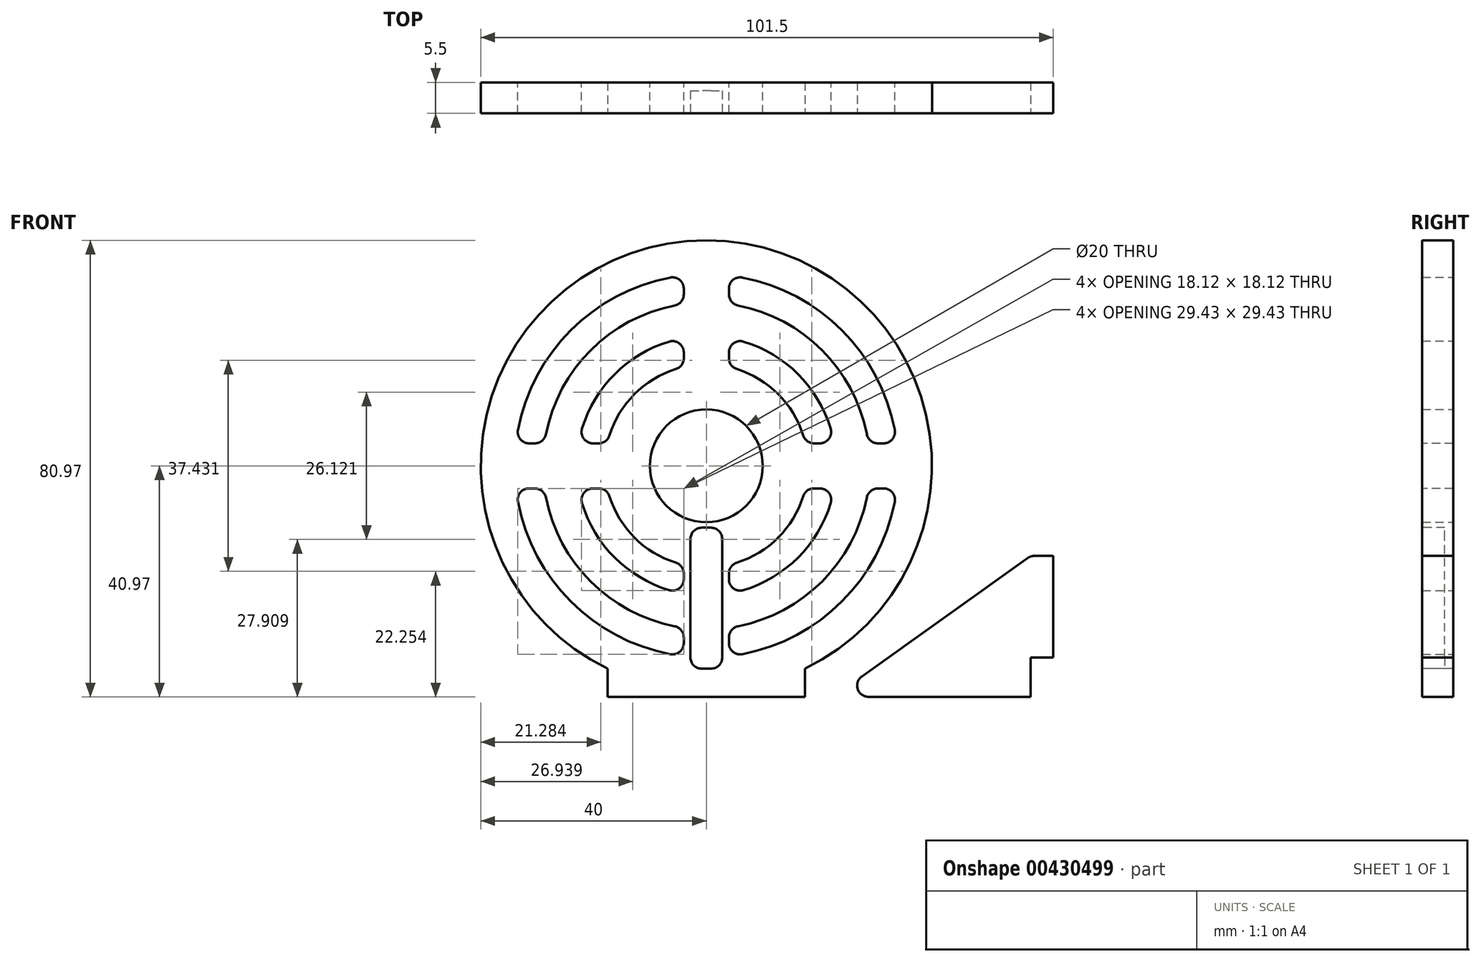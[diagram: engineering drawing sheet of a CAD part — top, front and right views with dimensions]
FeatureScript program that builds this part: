
annotation { "Feature Type Name" : "Feature", "Feature Type Description" : "" }
export const myFeature = defineFeature(function(context is Context, id is Id, definition is map)
    precondition{}
    {
        {
            var Q0;
            Q0=qCreatedBy(makeId("Front.planeOp"),FACE);
            var sketch = newSketch(context, id + "F0", { "sketchPlane" : qUnion([Q0])});
            skCircle(sketch, "E0", {"center": v(0, 0) * mm, "radius": 40 * mm});
            skLineSegment(sketch, "E1", {"start": v(0, 0) * mm, "end": v(-40, 0) * mm, "construction": true});
            skLineSegment(sketch, "E2", {"start": v(0, 0) * mm, "end": v(40, 0) * mm, "construction": true});
            skLineSegment(sketch, "E3", {"start": v(0, 0) * mm, "end": v(0, -40) * mm, "construction": true});
            skLineSegment(sketch, "E4", {"start": v(0, 0) * mm, "end": v(0, 23) * mm, "construction": true});
            skLineSegment(sketch, "E5.1", {"start": v(4, -17.55) * mm, "end": v(4, -22.65) * mm});
            skLineSegment(sketch, "E6.0", {"start": v(-4, 17.55) * mm, "end": v(-4, 22.65) * mm});
            skLineSegment(sketch, "E6.1", {"start": v(-4, -17.55) * mm, "end": v(-4, -22.65) * mm});
            skLineSegment(sketch, "E7.0", {"start": v(17.55, -4) * mm, "end": v(22.65, -4) * mm});
            skLineSegment(sketch, "E7.1", {"start": v(-17.55, -4) * mm, "end": v(-22.65, -4) * mm});
            skLineSegment(sketch, "E8.0", {"start": v(-17.55, 4) * mm, "end": v(-22.65, 4) * mm});
            skLineSegment(sketch, "E8.1", {"start": v(17.55, 4) * mm, "end": v(22.65, 4) * mm});
            skArc(sketch, "E9.0", {"start": v(-4, 33.76) * mm, "mid": v(-24.04, 24.04) * mm, "end": v(-33.76, 4) * mm});
            skArc(sketch, "E10.0", {"start": v(-4, 28.72) * mm, "mid": v(-20.5, 20.5) * mm, "end": v(-28.72, 4) * mm});
            skArc(sketch, "E11.0", {"start": v(-4, 22.65) * mm, "mid": v(-16.26, 16.26) * mm, "end": v(-22.65, 4) * mm});
            skArc(sketch, "E12.0", {"start": v(-4, 17.55) * mm, "mid": v(-12.73, 12.73) * mm, "end": v(-17.55, 4) * mm});
            skLineSegment(sketch, "E13.trimOffspring", {"start": v(-4, 28.72) * mm, "end": v(-4, 33.76) * mm});
            skLineSegment(sketch, "E14.trimOffspring", {"start": v(4, 28.72) * mm, "end": v(4, 33.76) * mm});
            skArc(sketch, "E15.trimOffspring", {"start": v(-17.55, -4) * mm, "mid": v(-12.73, -12.73) * mm, "end": v(-4, -17.55) * mm});
            skArc(sketch, "E16.trimOffspring", {"start": v(17.55, 4) * mm, "mid": v(12.73, 12.73) * mm, "end": v(4, 17.55) * mm});
            skArc(sketch, "E17.trimOffspring", {"start": v(22.65, 4) * mm, "mid": v(16.26, 16.26) * mm, "end": v(4, 22.65) * mm});
            skArc(sketch, "E18.trimOffspring", {"start": v(28.72, 4) * mm, "mid": v(20.5, 20.5) * mm, "end": v(4, 28.72) * mm});
            skArc(sketch, "E19.trimOffspring", {"start": v(33.76, 4) * mm, "mid": v(24.04, 24.04) * mm, "end": v(4, 33.76) * mm});
            skLineSegment(sketch, "E20.trimOffspring", {"start": v(28.72, -4) * mm, "end": v(33.76, -4) * mm});
            skLineSegment(sketch, "E21.trimOffspring", {"start": v(28.72, 4) * mm, "end": v(33.76, 4) * mm});
            skArc(sketch, "E22.trimOffspring", {"start": v(-33.76, -4) * mm, "mid": v(-24.04, -24.04) * mm, "end": v(-4, -33.76) * mm});
            skArc(sketch, "E23.trimOffspring", {"start": v(-28.72, -4) * mm, "mid": v(-20.5, -20.5) * mm, "end": v(-4, -28.72) * mm});
            skArc(sketch, "E24.trimOffspring", {"start": v(-22.65, -4) * mm, "mid": v(-16.26, -16.26) * mm, "end": v(-4, -22.65) * mm});
            skArc(sketch, "E25.trimOffspring", {"start": v(4, -22.65) * mm, "mid": v(16.26, -16.26) * mm, "end": v(22.65, -4) * mm});
            skArc(sketch, "E26.trimOffspring", {"start": v(4, -28.72) * mm, "mid": v(20.5, -20.5) * mm, "end": v(28.72, -4) * mm});
            skArc(sketch, "E27.trimOffspring", {"start": v(4, -33.76) * mm, "mid": v(24.04, -24.04) * mm, "end": v(33.76, -4) * mm});
            skLineSegment(sketch, "E28.trimOffspring", {"start": v(4, -28.72) * mm, "end": v(4, -33.76) * mm});
            skLineSegment(sketch, "E29.trimOffspring", {"start": v(-4, -28.72) * mm, "end": v(-4, -33.76) * mm});
            skPoint(sketch, "E30.orphan", {"position": v(-95.2, 0) * mm});
            skLineSegment(sketch, "E31.trimOffspring", {"start": v(-28.72, 4) * mm, "end": v(-33.76, 4) * mm});
            skLineSegment(sketch, "E32.trimOffspring", {"start": v(-28.72, -4) * mm, "end": v(-33.76, -4) * mm});
            skLineSegment(sketch, "E33.trimOffspring", {"start": v(4, 17.55) * mm, "end": v(4, 22.65) * mm});
            skArc(sketch, "E34.trimOffspring", {"start": v(4, -17.55) * mm, "mid": v(12.73, -12.73) * mm, "end": v(17.55, -4) * mm});
            skCircle(sketch, "E35", {"center": v(0, 0) * mm, "radius": 10 * mm});
            skSolve(sketch);
        }
        {
            var Q0;
            Q0 = qSketchRegion(id + "F0", true);
            extrude(context, id + "F1", {"entities" : qUnion([Q0]), "endBound" : BoundingType.SYMMETRIC, "depth" : 5.5 * mm});
        }
        {
            var Q0;
            Q0=makeQuery(id+"F1.opExtrude","CAP_FACE",FACE,{"disambiguationData":[OSD([sQuery(id+"F0.wireOp",EDGE,"E0"),sQuery(id+"F0.wireOp",EDGE,"E5.1"),sQuery(id+"F0.wireOp",EDGE,"E6.0"),sQuery(id+"F0.wireOp",EDGE,"E6.1"),sQuery(id+"F0.wireOp",EDGE,"E7.0"),sQuery(id+"F0.wireOp",EDGE,"E7.1"),sQuery(id+"F0.wireOp",EDGE,"E8.0"),sQuery(id+"F0.wireOp",EDGE,"E8.1"),sQuery(id+"F0.wireOp",EDGE,"E9.0"),sQuery(id+"F0.wireOp",EDGE,"E10.0"),sQuery(id+"F0.wireOp",EDGE,"E11.0"),sQuery(id+"F0.wireOp",EDGE,"E12.0"),sQuery(id+"F0.wireOp",EDGE,"E13.trimOffspring"),sQuery(id+"F0.wireOp",EDGE,"E14.trimOffspring"),sQuery(id+"F0.wireOp",EDGE,"36b8c476-04b0-4987-b28c-c769265a3c3a.trimOffspring"),sQuery(id+"F0.wireOp",EDGE,"E15.trimOffspring"),sQuery(id+"F0.wireOp",EDGE,"E16.trimOffspring"),sQuery(id+"F0.wireOp",EDGE,"E17.trimOffspring"),sQuery(id+"F0.wireOp",EDGE,"E18.trimOffspring"),sQuery(id+"F0.wireOp",EDGE,"E19.trimOffspring"),sQuery(id+"F0.wireOp",EDGE,"E20.trimOffspring"),sQuery(id+"F0.wireOp",EDGE,"E21.trimOffspring"),sQuery(id+"F0.wireOp",EDGE,"E22.trimOffspring"),sQuery(id+"F0.wireOp",EDGE,"E23.trimOffspring"),sQuery(id+"F0.wireOp",EDGE,"E24.trimOffspring"),sQuery(id+"F0.wireOp",EDGE,"E25.trimOffspring"),sQuery(id+"F0.wireOp",EDGE,"E26.trimOffspring"),sQuery(id+"F0.wireOp",EDGE,"E27.trimOffspring"),sQuery(id+"F0.wireOp",EDGE,"E28.trimOffspring"),sQuery(id+"F0.wireOp",EDGE,"E29.trimOffspring"),sQuery(id+"F0.wireOp",EDGE,"E31.trimOffspring"),sQuery(id+"F0.wireOp",EDGE,"E32.trimOffspring")])],"isStart":false});
            var sketch = newSketch(context, id + "F2", { "sketchPlane" : qUnion([Q0])});
            skLineSegment(sketch, "E36", {"start": v(-17.5, -35.97) * mm, "end": v(-17.5, -40.97) * mm});
            skLineSegment(sketch, "E37", {"start": v(-17.5, -40.97) * mm, "end": v(17.5, -40.97) * mm});
            skLineSegment(sketch, "E38", {"start": v(17.5, -40.97) * mm, "end": v(17.5, -35.97) * mm});
            skArc(sketch, "E39.0", {"start": v(-17.5, -35.97) * mm, "mid": v(0, -40) * mm, "end": v(17.5, -35.97) * mm});
            skLineSegment(sketch, "E40", {"start": v(0, -40.97) * mm, "end": v(0, 0) * mm, "construction": true});
            skSolve(sketch);
        }
        {
            var Q0;
            Q0 = qSketchRegion(id + "F2", true);
            extrude(context, id + "F3", {"entities" : qUnion([Q0]), "operationType" : NewBodyOperationType.ADD, "oppositeDirection" : true, "depth" : 5.5 * mm});
        }
        {
            var Q0;
            Q0=makeQuery(id+"F3.boolean.opBoolean","MERGE",FACE,{"derivedFrom":[makeQuery(id+"F1.opExtrude","CAP_FACE",FACE,{"disambiguationData":[OSD([sQuery(id+"F0.wireOp",EDGE,"E0"),sQuery(id+"F0.wireOp",EDGE,"E5.1"),sQuery(id+"F0.wireOp",EDGE,"E6.0"),sQuery(id+"F0.wireOp",EDGE,"E6.1"),sQuery(id+"F0.wireOp",EDGE,"E7.0"),sQuery(id+"F0.wireOp",EDGE,"E7.1"),sQuery(id+"F0.wireOp",EDGE,"E8.0"),sQuery(id+"F0.wireOp",EDGE,"E8.1"),sQuery(id+"F0.wireOp",EDGE,"E9.0"),sQuery(id+"F0.wireOp",EDGE,"E10.0"),sQuery(id+"F0.wireOp",EDGE,"E11.0"),sQuery(id+"F0.wireOp",EDGE,"E12.0"),sQuery(id+"F0.wireOp",EDGE,"E13.trimOffspring"),sQuery(id+"F0.wireOp",EDGE,"E14.trimOffspring"),sQuery(id+"F0.wireOp",EDGE,"36b8c476-04b0-4987-b28c-c769265a3c3a.trimOffspring"),sQuery(id+"F0.wireOp",EDGE,"E15.trimOffspring"),sQuery(id+"F0.wireOp",EDGE,"E16.trimOffspring"),sQuery(id+"F0.wireOp",EDGE,"E17.trimOffspring"),sQuery(id+"F0.wireOp",EDGE,"E18.trimOffspring"),sQuery(id+"F0.wireOp",EDGE,"E19.trimOffspring"),sQuery(id+"F0.wireOp",EDGE,"E20.trimOffspring"),sQuery(id+"F0.wireOp",EDGE,"E21.trimOffspring"),sQuery(id+"F0.wireOp",EDGE,"E22.trimOffspring"),sQuery(id+"F0.wireOp",EDGE,"E23.trimOffspring"),sQuery(id+"F0.wireOp",EDGE,"E24.trimOffspring"),sQuery(id+"F0.wireOp",EDGE,"E25.trimOffspring"),sQuery(id+"F0.wireOp",EDGE,"E26.trimOffspring"),sQuery(id+"F0.wireOp",EDGE,"E27.trimOffspring"),sQuery(id+"F0.wireOp",EDGE,"E28.trimOffspring"),sQuery(id+"F0.wireOp",EDGE,"E29.trimOffspring"),sQuery(id+"F0.wireOp",EDGE,"E31.trimOffspring"),sQuery(id+"F0.wireOp",EDGE,"E32.trimOffspring")])],"isStart":false}),makeQuery(id+"F3.opExtrude","CAP_FACE",FACE,{"disambiguationData":[OSD([sQuery(id+"F2.wireOp",EDGE,"E36"),sQuery(id+"F2.wireOp",EDGE,"E37"),sQuery(id+"F2.wireOp",EDGE,"E38"),sQuery(id+"F2.wireOp",EDGE,"E39.0")])],"isStart":true})]});
            var sketch = newSketch(context, id + "F4", { "sketchPlane" : qUnion([Q0])});
            skLineSegment(sketch, "E41", {"start": v(22.5, -40.97) * mm, "end": v(57.5, -15.97) * mm});
            skLineSegment(sketch, "E42", {"start": v(57.5, -15.97) * mm, "end": v(57.5, -40.97) * mm});
            skLineSegment(sketch, "E43", {"start": v(57.5, -40.97) * mm, "end": v(22.5, -40.97) * mm});
            skSolve(sketch);
        }
        {
            var Q0;
            Q0 = qSketchRegion(id + "F4", true);
            extrude(context, id + "F5", {"entities" : qUnion([Q0]), "oppositeDirection" : true, "depth" : 5.5 * mm});
        }
        {
            var Q0;
            Q0=makeQuery(id+"F1.opExtrude","SWEPT_EDGE",EDGE,{"disambiguationData":[OSD([sQuery(id+"F0.wireOp",EDGE,"E8.1"),sQuery(id+"F0.wireOp",EDGE,"E16.trimOffspring")])]});
            var Q1;
            Q1=makeQuery(id+"F1.opExtrude","SWEPT_EDGE",EDGE,{"disambiguationData":[OSD([sQuery(id+"F0.wireOp",EDGE,"36b8c476-04b0-4987-b28c-c769265a3c3a.trimOffspring"),sQuery(id+"F0.wireOp",EDGE,"E16.trimOffspring")])]});
            var Q2;
            Q2=makeQuery(id+"F1.opExtrude","SWEPT_EDGE",EDGE,{"disambiguationData":[OSD([sQuery(id+"F0.wireOp",EDGE,"E18.trimOffspring"),sQuery(id+"F0.wireOp",EDGE,"E21.trimOffspring")])]});
            var Q3;
            Q3=makeQuery(id+"F1.opExtrude","SWEPT_EDGE",EDGE,{"disambiguationData":[OSD([sQuery(id+"F0.wireOp",EDGE,"E14.trimOffspring"),sQuery(id+"F0.wireOp",EDGE,"E18.trimOffspring")])]});
            var Q4;
            Q4=makeQuery(id+"F1.opExtrude","SWEPT_EDGE",EDGE,{"disambiguationData":[OSD([sQuery(id+"F0.wireOp",EDGE,"E8.0"),sQuery(id+"F0.wireOp",EDGE,"E11.0")])]});
            var Q5;
            Q5=makeQuery(id+"F1.opExtrude","SWEPT_EDGE",EDGE,{"disambiguationData":[OSD([sQuery(id+"F0.wireOp",EDGE,"E10.0"),sQuery(id+"F0.wireOp",EDGE,"E13.trimOffspring")])]});
            var Q6;
            Q6=makeQuery(id+"F1.opExtrude","SWEPT_EDGE",EDGE,{"disambiguationData":[OSD([sQuery(id+"F0.wireOp",EDGE,"E10.0"),sQuery(id+"F0.wireOp",EDGE,"E31.trimOffspring")])]});
            var Q7;
            Q7=makeQuery(id+"F1.opExtrude","SWEPT_EDGE",EDGE,{"disambiguationData":[OSD([sQuery(id+"F0.wireOp",EDGE,"E8.0"),sQuery(id+"F0.wireOp",EDGE,"E12.0")])]});
            var Q8;
            Q8=makeQuery(id+"F1.opExtrude","SWEPT_EDGE",EDGE,{"disambiguationData":[OSD([sQuery(id+"F0.wireOp",EDGE,"E6.0"),sQuery(id+"F0.wireOp",EDGE,"E12.0")])]});
            var Q9;
            Q9=makeQuery(id+"F1.opExtrude","SWEPT_EDGE",EDGE,{"disambiguationData":[OSD([sQuery(id+"F0.wireOp",EDGE,"E14.trimOffspring"),sQuery(id+"F0.wireOp",EDGE,"E19.trimOffspring")])]});
            var Q10;
            Q10=makeQuery(id+"F1.opExtrude","SWEPT_EDGE",EDGE,{"disambiguationData":[OSD([sQuery(id+"F0.wireOp",EDGE,"E19.trimOffspring"),sQuery(id+"F0.wireOp",EDGE,"E21.trimOffspring")])]});
            var Q11;
            Q11=makeQuery(id+"F1.opExtrude","SWEPT_EDGE",EDGE,{"disambiguationData":[OSD([sQuery(id+"F0.wireOp",EDGE,"E9.0"),sQuery(id+"F0.wireOp",EDGE,"E13.trimOffspring")])]});
            var Q12;
            Q12=makeQuery(id+"F1.opExtrude","SWEPT_EDGE",EDGE,{"disambiguationData":[OSD([sQuery(id+"F0.wireOp",EDGE,"E9.0"),sQuery(id+"F0.wireOp",EDGE,"E31.trimOffspring")])]});
            var Q13;
            Q13=makeQuery(id+"F1.opExtrude","SWEPT_EDGE",EDGE,{"disambiguationData":[OSD([sQuery(id+"F0.wireOp",EDGE,"E7.1"),sQuery(id+"F0.wireOp",EDGE,"E15.trimOffspring")])]});
            var Q14;
            Q14=makeQuery(id+"F1.opExtrude","SWEPT_EDGE",EDGE,{"disambiguationData":[OSD([sQuery(id+"F0.wireOp",EDGE,"E23.trimOffspring"),sQuery(id+"F0.wireOp",EDGE,"E32.trimOffspring")])]});
            var Q15;
            Q15=makeQuery(id+"F1.opExtrude","SWEPT_EDGE",EDGE,{"disambiguationData":[OSD([sQuery(id+"F0.wireOp",EDGE,"E7.0"),sQuery(id+"F0.wireOp",EDGE,"E15.trimOffspring")])]});
            var Q16;
            Q16=makeQuery(id+"F1.opExtrude","SWEPT_EDGE",EDGE,{"disambiguationData":[OSD([sQuery(id+"F0.wireOp",EDGE,"E5.1"),sQuery(id+"F0.wireOp",EDGE,"E15.trimOffspring")])]});
            var Q17;
            Q17=makeQuery(id+"F1.opExtrude","SWEPT_EDGE",EDGE,{"disambiguationData":[OSD([sQuery(id+"F0.wireOp",EDGE,"E20.trimOffspring"),sQuery(id+"F0.wireOp",EDGE,"E26.trimOffspring")])]});
            var Q18;
            Q18=makeQuery(id+"F1.opExtrude","SWEPT_EDGE",EDGE,{"disambiguationData":[OSD([sQuery(id+"F0.wireOp",EDGE,"E26.trimOffspring"),sQuery(id+"F0.wireOp",EDGE,"E28.trimOffspring")])]});
            var Q19;
            Q19=makeQuery(id+"F1.opExtrude","SWEPT_EDGE",EDGE,{"disambiguationData":[OSD([sQuery(id+"F0.wireOp",EDGE,"E20.trimOffspring"),sQuery(id+"F0.wireOp",EDGE,"E27.trimOffspring")])]});
            var Q20;
            Q20=makeQuery(id+"F1.opExtrude","SWEPT_EDGE",EDGE,{"disambiguationData":[OSD([sQuery(id+"F0.wireOp",EDGE,"E7.0"),sQuery(id+"F0.wireOp",EDGE,"E25.trimOffspring")])]});
            var Q21;
            Q21=makeQuery(id+"F1.opExtrude","SWEPT_EDGE",EDGE,{"disambiguationData":[OSD([sQuery(id+"F0.wireOp",EDGE,"E23.trimOffspring"),sQuery(id+"F0.wireOp",EDGE,"E29.trimOffspring")])]});
            var Q22;
            Q22=makeQuery(id+"F1.opExtrude","SWEPT_EDGE",EDGE,{"disambiguationData":[OSD([sQuery(id+"F0.wireOp",EDGE,"E22.trimOffspring"),sQuery(id+"F0.wireOp",EDGE,"E32.trimOffspring")])]});
            var Q23;
            Q23=makeQuery(id+"F1.opExtrude","SWEPT_EDGE",EDGE,{"disambiguationData":[OSD([sQuery(id+"F0.wireOp",EDGE,"E7.1"),sQuery(id+"F0.wireOp",EDGE,"E24.trimOffspring")])]});
            var Q24;
            Q24=makeQuery(id+"F1.opExtrude","SWEPT_EDGE",EDGE,{"disambiguationData":[OSD([sQuery(id+"F0.wireOp",EDGE,"E22.trimOffspring"),sQuery(id+"F0.wireOp",EDGE,"E29.trimOffspring")])]});
            var Q25;
            Q25=makeQuery(id+"F1.opExtrude","SWEPT_EDGE",EDGE,{"disambiguationData":[OSD([sQuery(id+"F0.wireOp",EDGE,"E27.trimOffspring"),sQuery(id+"F0.wireOp",EDGE,"E28.trimOffspring")])]});
            var Q26;
            Q26=makeQuery(id+"F1.opExtrude","SWEPT_EDGE",EDGE,{"disambiguationData":[OSD([sQuery(id+"F0.wireOp",EDGE,"E8.1"),sQuery(id+"F0.wireOp",EDGE,"E17.trimOffspring")])]});
            var Q27;
            Q27=makeQuery(id+"F1.opExtrude","SWEPT_EDGE",EDGE,{"disambiguationData":[OSD([sQuery(id+"F0.wireOp",EDGE,"E6.0"),sQuery(id+"F0.wireOp",EDGE,"E11.0")])]});
            var Q28;
            Q28=makeQuery(id+"F1.opExtrude","SWEPT_EDGE",EDGE,{"disambiguationData":[OSD([sQuery(id+"F0.wireOp",EDGE,"36b8c476-04b0-4987-b28c-c769265a3c3a.trimOffspring"),sQuery(id+"F0.wireOp",EDGE,"E17.trimOffspring")])]});
            var Q29;
            Q29=makeQuery(id+"F1.opExtrude","SWEPT_EDGE",EDGE,{"disambiguationData":[OSD([sQuery(id+"F0.wireOp",EDGE,"E6.1"),sQuery(id+"F0.wireOp",EDGE,"E15.trimOffspring")])]});
            var Q30;
            Q30=makeQuery(id+"F1.opExtrude","SWEPT_EDGE",EDGE,{"disambiguationData":[OSD([sQuery(id+"F0.wireOp",EDGE,"E5.1"),sQuery(id+"F0.wireOp",EDGE,"E25.trimOffspring")])]});
            var Q31;
            Q31=makeQuery(id+"F1.opExtrude","SWEPT_EDGE",EDGE,{"disambiguationData":[OSD([sQuery(id+"F0.wireOp",EDGE,"E6.1"),sQuery(id+"F0.wireOp",EDGE,"E24.trimOffspring")])]});
            var Q32;
            Q32=makeQuery(id+"F3.opExtrude","SWEPT_EDGE",EDGE,{"disambiguationData":[OSD([sQuery(id+"F0.wireOp",EDGE,"E0"),sQuery(id+"F2.wireOp",EDGE,"E36"),sQuery(id+"F2.wireOp",EDGE,"E39.0")])]});
            var Q33;
            Q33=makeQuery(id+"F3.opExtrude","SWEPT_EDGE",EDGE,{"disambiguationData":[OSD([sQuery(id+"F0.wireOp",EDGE,"E0"),sQuery(id+"F2.wireOp",EDGE,"E38"),sQuery(id+"F2.wireOp",EDGE,"E39.0")])]});
            fillet(context, id + "F6", {"entities" : qUnion([Q0, Q1, Q2, Q3, Q4, Q5, Q6, Q7, Q8, Q9, Q10, Q11, Q12, Q13, Q14, Q15, Q16, Q17, Q18, Q19, Q20, Q21, Q22, Q23, Q24, Q25, Q26, Q27, Q28, Q29, Q30, Q31, Q32, Q33]), "radius" : 2 * mm, "tangentPropagation" : true, "allowEdgeOverflow" : false});
        }
        {
            var Q0;
            Q0=makeQuery(id+"F5.opExtrude","CAP_FACE",FACE,{"disambiguationData":[OSD([sQuery(id+"F4.wireOp",EDGE,"E41"),sQuery(id+"F4.wireOp",EDGE,"E42"),sQuery(id+"F4.wireOp",EDGE,"E43")])],"isStart":true});
            var sketch = newSketch(context, id + "F7", { "sketchPlane" : qUnion([Q0])});
            skLineSegment(sketch, "E44", {"start": v(57.5, -15.97) * mm, "end": v(61.5, -15.97) * mm});
            skLineSegment(sketch, "E45", {"start": v(61.5, -15.97) * mm, "end": v(61.5, -33.97) * mm});
            skLineSegment(sketch, "E46", {"start": v(61.5, -33.97) * mm, "end": v(57.5, -33.97) * mm});
            skLineSegment(sketch, "E47", {"start": v(57.5, -33.97) * mm, "end": v(57.5, -15.97) * mm});
            skSolve(sketch);
        }
        {
            var Q0;
            Q0 = qSketchRegion(id + "F7", true);
            extrude(context, id + "F8", {"entities" : qUnion([Q0]), "operationType" : NewBodyOperationType.ADD, "oppositeDirection" : true, "depth" : 5.5 * mm});
        }
        {
            var Q0;
            Q0=makeQuery(id+"F8.opExtrude","SWEPT_EDGE",EDGE,{"disambiguationData":[OSD([sQuery(id+"F4.wireOp",EDGE,"E42"),sQuery(id+"F7.wireOp",EDGE,"E46"),sQuery(id+"F7.wireOp",EDGE,"E47")])]});
            var Q1;
            Q1=makeQuery(id+"F5.opExtrude","SWEPT_EDGE",EDGE,{"disambiguationData":[OSD([sQuery(id+"F4.wireOp",EDGE,"E41"),sQuery(id+"F4.wireOp",EDGE,"E43")])]});
            var Q2;
            {var subQ0=sQuery(id+"F4.wireOp",EDGE,"E41");Q2=makeQuery(id+"F8.boolean.opBoolean","MERGE",EDGE,{"derivedFrom":[makeQuery(id+"F5.opExtrude","SWEPT_EDGE",EDGE,{"disambiguationData":[OSD([subQ0,sQuery(id+"F4.wireOp",EDGE,"E42")])]}),makeQuery(id+"F8.opExtrude","SWEPT_EDGE",EDGE,{"disambiguationData":[OSD([subQ0,sQuery(id+"F7.wireOp",EDGE,"E44"),sQuery(id+"F7.wireOp",EDGE,"E47")])]})]});}
            fillet(context, id + "F9", {"entities" : qUnion([Q0, Q1, Q2]), "radius" : 2 * mm, "tangentPropagation" : true, "allowEdgeOverflow" : false});
        }
        {
            var Q0;
            Q0=makeQuery(id+"F3.boolean.opBoolean","MERGE",FACE,{"derivedFrom":[makeQuery(id+"F1.opExtrude","CAP_FACE",FACE,{"disambiguationData":[OSD([sQuery(id+"F0.wireOp",EDGE,"E0"),sQuery(id+"F0.wireOp",EDGE,"E5.1"),sQuery(id+"F0.wireOp",EDGE,"E6.0"),sQuery(id+"F0.wireOp",EDGE,"E6.1"),sQuery(id+"F0.wireOp",EDGE,"E7.0"),sQuery(id+"F0.wireOp",EDGE,"E7.1"),sQuery(id+"F0.wireOp",EDGE,"E8.0"),sQuery(id+"F0.wireOp",EDGE,"E8.1"),sQuery(id+"F0.wireOp",EDGE,"E9.0"),sQuery(id+"F0.wireOp",EDGE,"E10.0"),sQuery(id+"F0.wireOp",EDGE,"E11.0"),sQuery(id+"F0.wireOp",EDGE,"E12.0"),sQuery(id+"F0.wireOp",EDGE,"E13.trimOffspring"),sQuery(id+"F0.wireOp",EDGE,"E14.trimOffspring"),sQuery(id+"F0.wireOp",EDGE,"36b8c476-04b0-4987-b28c-c769265a3c3a.trimOffspring"),sQuery(id+"F0.wireOp",EDGE,"E15.trimOffspring"),sQuery(id+"F0.wireOp",EDGE,"E16.trimOffspring"),sQuery(id+"F0.wireOp",EDGE,"E17.trimOffspring"),sQuery(id+"F0.wireOp",EDGE,"E18.trimOffspring"),sQuery(id+"F0.wireOp",EDGE,"E19.trimOffspring"),sQuery(id+"F0.wireOp",EDGE,"E20.trimOffspring"),sQuery(id+"F0.wireOp",EDGE,"E21.trimOffspring"),sQuery(id+"F0.wireOp",EDGE,"E22.trimOffspring"),sQuery(id+"F0.wireOp",EDGE,"E23.trimOffspring"),sQuery(id+"F0.wireOp",EDGE,"E24.trimOffspring"),sQuery(id+"F0.wireOp",EDGE,"E25.trimOffspring"),sQuery(id+"F0.wireOp",EDGE,"E26.trimOffspring"),sQuery(id+"F0.wireOp",EDGE,"E27.trimOffspring"),sQuery(id+"F0.wireOp",EDGE,"E28.trimOffspring"),sQuery(id+"F0.wireOp",EDGE,"E29.trimOffspring"),sQuery(id+"F0.wireOp",EDGE,"E31.trimOffspring"),sQuery(id+"F0.wireOp",EDGE,"E32.trimOffspring")])],"isStart":false}),makeQuery(id+"F3.opExtrude","CAP_FACE",FACE,{"disambiguationData":[OSD([sQuery(id+"F2.wireOp",EDGE,"E36"),sQuery(id+"F2.wireOp",EDGE,"E37"),sQuery(id+"F2.wireOp",EDGE,"E38"),sQuery(id+"F2.wireOp",EDGE,"E39.0")])],"isStart":true})]});
            var sketch = newSketch(context, id + "F10", { "sketchPlane" : qUnion([Q0])});
            skLineSegment(sketch, "E48", {"start": v(0, 0) * mm, "end": v(0, -40.97) * mm, "construction": true});
            skLineSegment(sketch, "E49.bottom", {"start": v(2.83, -35.97) * mm, "end": v(-2.82, -35.97) * mm});
            skLineSegment(sketch, "E49.top", {"start": v(2.83, -10.97) * mm, "end": v(-2.82, -10.97) * mm});
            skLineSegment(sketch, "E49.left", {"start": v(2.83, -35.97) * mm, "end": v(2.83, -10.97) * mm});
            skLineSegment(sketch, "E49.right", {"start": v(-2.82, -35.97) * mm, "end": v(-2.82, -10.97) * mm});
            skPoint(sketch, "E49.middle", {"position": v(0, -23.47) * mm});
            skSolve(sketch);
        }
        {
            var Q0;
            Q0 = qSketchRegion(id + "F10", true);
            extrude(context, id + "F11", {"entities" : qUnion([Q0]), "operationType" : NewBodyOperationType.REMOVE, "oppositeDirection" : true, "depth" : 4 * mm});
        }
        {
            var Q0;
            Q0=makeQuery(id+"F11.boolean.opBoolean","COPY",EDGE,{"derivedFrom":makeQuery(id+"F11.opExtrude","SWEPT_EDGE",EDGE,{"disambiguationData":[OSD([sQuery(id+"F10.wireOp",EDGE,"E49.top"),sQuery(id+"F10.wireOp",EDGE,"E49.right")])]})});
            var Q1;
            Q1=makeQuery(id+"F11.boolean.opBoolean","COPY",EDGE,{"derivedFrom":makeQuery(id+"F11.opExtrude","SWEPT_EDGE",EDGE,{"disambiguationData":[OSD([sQuery(id+"F10.wireOp",EDGE,"E49.top"),sQuery(id+"F10.wireOp",EDGE,"E49.left")])]})});
            var Q2;
            Q2=makeQuery(id+"F11.boolean.opBoolean","COPY",EDGE,{"derivedFrom":makeQuery(id+"F11.opExtrude","SWEPT_EDGE",EDGE,{"disambiguationData":[OSD([sQuery(id+"F10.wireOp",EDGE,"E49.bottom"),sQuery(id+"F10.wireOp",EDGE,"E49.left")])]})});
            var Q3;
            Q3=makeQuery(id+"F11.boolean.opBoolean","COPY",EDGE,{"derivedFrom":makeQuery(id+"F11.opExtrude","SWEPT_EDGE",EDGE,{"disambiguationData":[OSD([sQuery(id+"F10.wireOp",EDGE,"E49.bottom"),sQuery(id+"F10.wireOp",EDGE,"E49.right")])]})});
            fillet(context, id + "F12", {"entities" : qUnion([Q0, Q1, Q2, Q3]), "radius" : 2 * mm, "tangentPropagation" : true, "allowEdgeOverflow" : false});
        }
    });
